# Revit family: WHDG-5RD
name_source: partatom
category: Plumbing Fixtures
revit_build: Autodesk Revit 2018 (Build: 20170223_1515(x64)
units: mm (PartAtom-declared; Revit-internal decimal feet)

## family parameters
Always vertical = No
Cut with Voids When Loaded = No
OmniClass Number = 23.70.50.21.24
OmniClass Title = Waste Water Drains
Part Type = Normal
Room Calculation Point = No
Round Connector Dimension = Use Diameter
Shared = Yes
Work Plane-Based = Yes

## types (1)
- WHDG-5RD
    Assembly Code = D2030
    CW Connection = No
    Default Elevation = 0"
    Description = Ligature Resistant Floor Drain Grate
    Diameter = 5"
    Drain Material = Metal-Whitehall-Ligature Resistant Nickel Bronze
    HW Connection = No
    Installation Type = Floor
    Manufacturer = Whitehall Mfg.
    Model = WHDG-5RD
    Product Documentation Link = https://www.whitehallmfg.com
    Product Page URL = https://www.whitehallmfg.com
    Type Comments = For use in JR SMITH Floor Drains
    URL = https://www.whitehallmfg.com
    Vent Connection = No
    Waste Connection = No

## geometry (parser evidence)
native form markers: Sweep x2
no freeform markers — native parametric forms only
